# Revit family: Bath_Mixer-GROHE-Eurocube-23672000
name_source: partatom
category: Plumbing Fixtures
revit_build: Autodesk Revit 2014 (Build: 20130308_1515(x64)
units: mm (PartAtom-declared; Revit-internal decimal feet)

## types (6) — shared parameters
Assembly Code = D2020300
CW Connection = Yes
CWFU = 3
Cold Water Connection Diameter = 1/2"
Default Elevation = 0"
Description = Square Floor Mount Tub Filler
HW Connection = Yes
HWFU = 3
Height = 32 5/8"
Hot Water Connection Diameter = 1"
Installation Type = Floor Mounted
Length = 7 3/8"
Manufacturer = DXV
Price = Prices may vary. Please consult Manufacturer Representative for most up-to-date price list.
Product Documentation Link = https://dxv01.blob.core.windows.net
Product Page URL = https://www.dxv.com
Tempered Water Connection Diameter = 1/2"
Vent Connection = No
WFU = 4
Warranty Documentation Link = https://www.dxv.com
Waste Connection = No
Width = 7 13/16"

## per-type parameters (varying)
| type | Flow Rate | Materials |
| D35900900.100 | 2.0 gpm (7.6 L/min) | Cast Brass-DXV-100-Polished Chrome |
| D35900900C.100 | 1.8 gpm (6.8 L/min) | Cast Brass-DXV-100-Polished Chrome |
| D35900900.144 | 2.0 gpm (7.6 L/min) | Cast Brass-DXV-144-Brushed Nickel |
| D35900900C.144 | 1.8 gpm (6.8 L/min) | Cast Brass-DXV-144-Brushed Nickel |
| D35900900.243 | 2.0 gpm (7.6 L/min) | Cast Brass-DXV-243-Matte Black |
| D35900900C.243 | 1.8 gpm (6.8 L/min) | Cast Brass-DXV-243-Matte Black |

note: column(s) folded — value = type name in every type: Model

## geometry (parser evidence)
native form markers: Sweep x1
no freeform markers — native parametric forms only
